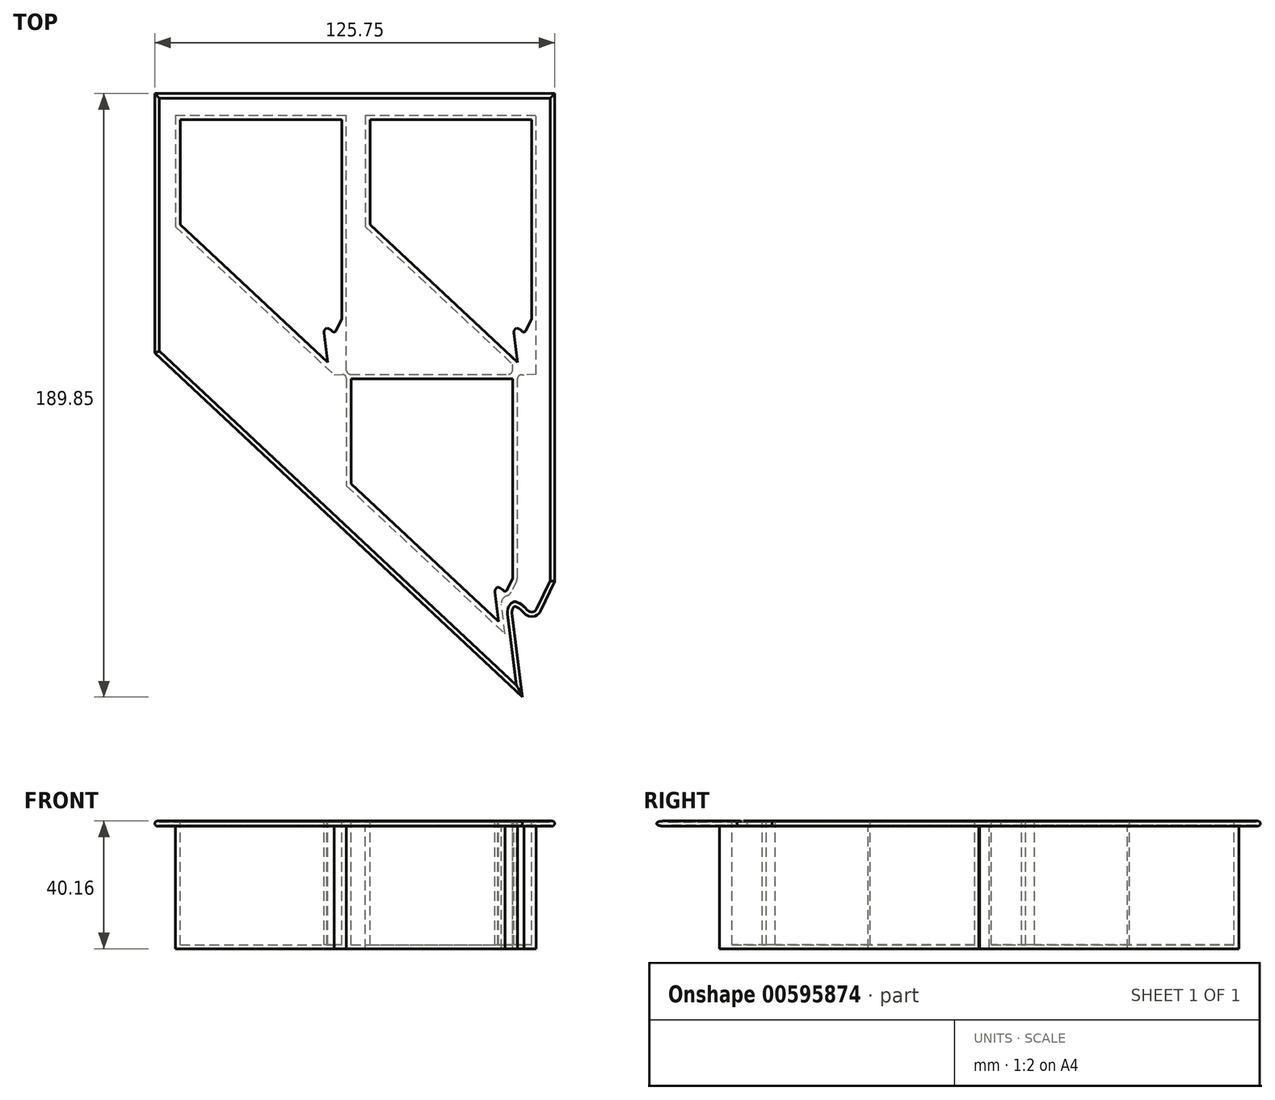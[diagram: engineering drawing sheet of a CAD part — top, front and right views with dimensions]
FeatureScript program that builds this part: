
annotation { "Feature Type Name" : "Feature", "Feature Type Description" : "" }
export const myFeature = defineFeature(function(context is Context, id is Id, definition is map)
    precondition{}
    {
        {
            var Q0;
            Q0=qCreatedBy(makeId("Top.planeOp"),FACE);
            var sketch = newSketch(context, id + "F0", { "sketchPlane" : qUnion([Q0])});
            skLineSegment(sketch, "E0.0.1.0", {"start": v(5.08, 168.36) * mm, "end": v(5.08, 133.3) * mm});
            skLineSegment(sketch, "E0.0.1.1", {"start": v(5.08, 133.3) * mm, "end": v(54.96, 86.61) * mm});
            skLineSegment(sketch, "E0.0.1.2", {"start": v(6.58, 133.95) * mm, "end": v(52.95, 90.55) * mm});
            skLineSegment(sketch, "E0.0.1.3", {"start": v(6.58, 166.86) * mm, "end": v(57.33, 166.86) * mm});
            skLineSegment(sketch, "E0.0.1.4", {"start": v(57.33, 104.15) * mm, "end": v(57.33, 166.86) * mm});
            skLineSegment(sketch, "E0.0.1.5", {"start": v(6.58, 166.86) * mm, "end": v(6.58, 133.95) * mm});
            skLineSegment(sketch, "E0.0.1.6", {"start": v(58.83, 104.4) * mm, "end": v(58.83, 168.36) * mm});
            skLineSegment(sketch, "E0.0.1.7", {"start": v(5.08, 168.36) * mm, "end": v(58.83, 168.36) * mm});
            skPoint(sketch, "E0.0.1.8", {"position": v(51.57, 101.26) * mm});
            skPoint(sketch, "E0.0.1.9", {"position": v(53.31, 101.48) * mm});
            skPoint(sketch, "E0.0.1.10", {"position": v(58.83, 103.8) * mm});
            skLineSegment(sketch, "E0.0.1.11", {"start": v(54.96, 86.61) * mm, "end": v(53.77, 95.92) * mm});
            skLineSegment(sketch, "E0.0.1.12", {"start": v(52.95, 90.55) * mm, "end": v(51.76, 99.78) * mm});
            skPoint(sketch, "E0.0.1.13", {"position": v(53, 101.9) * mm});
            skPoint(sketch, "E0.0.1.14", {"position": v(55.08, 99.52) * mm});
            skArc(sketch, "E0.0.1.15", {"start": v(55.55, 98.67) * mm, "mid": v(54.15, 97.62) * mm, "end": v(53.77, 95.92) * mm});
            skArc(sketch, "E0.0.1.16", {"start": v(53.06, 101.45) * mm, "mid": v(52.06, 100.88) * mm, "end": v(51.76, 99.78) * mm});
            skLineSegment(sketch, "E0.0.1.17", {"start": v(58.57, 103.28) * mm, "end": v(56.89, 99.82) * mm});
            skArc(sketch, "E0.0.1.18", {"start": v(58.57, 103.28) * mm, "mid": v(58.76, 103.82) * mm, "end": v(58.83, 104.4) * mm});
            skArc(sketch, "E0.0.1.19", {"start": v(54.13, 100.58) * mm, "mid": v(53.2, 101.2) * mm, "end": v(52.1, 101.33) * mm});
            skArc(sketch, "E0.0.1.20", {"start": v(55.55, 98.67) * mm, "mid": v(56.34, 99.1) * mm, "end": v(56.89, 99.82) * mm});
            skLineSegment(sketch, "E0.0.1.21", {"start": v(52.1, 101.33) * mm, "end": v(53.06, 101.45) * mm});
            skArc(sketch, "E0.0.1.22", {"start": v(54.37, 100.3) * mm, "mid": v(55, 100.08) * mm, "end": v(55.54, 100.47) * mm});
            skLineSegment(sketch, "E0.0.1.23", {"start": v(57.33, 104.15) * mm, "end": v(55.54, 100.47) * mm});
            skLineSegment(sketch, "E0.0.1.24", {"start": v(54.13, 100.58) * mm, "end": v(54.37, 100.3) * mm});
            skLineSegment(sketch, "E0.1.0.0", {"start": v(58.83, 85.48) * mm, "end": v(58.83, 51.77) * mm});
            skLineSegment(sketch, "E0.1.0.1", {"start": v(58.83, 51.77) * mm, "end": v(108.71, 5.08) * mm});
            skLineSegment(sketch, "E0.1.0.2", {"start": v(60.33, 52.42) * mm, "end": v(106.7, 9.02) * mm});
            skLineSegment(sketch, "E0.1.0.3", {"start": v(60.33, 85.33) * mm, "end": v(111.08, 85.33) * mm});
            skLineSegment(sketch, "E0.1.0.4", {"start": v(111.08, 22.62) * mm, "end": v(111.08, 85.33) * mm});
            skLineSegment(sketch, "E0.1.0.5", {"start": v(60.33, 85.33) * mm, "end": v(60.33, 52.42) * mm});
            skLineSegment(sketch, "E0.1.0.6", {"start": v(112.58, 22.86) * mm, "end": v(112.58, 85.34) * mm});
            skLineSegment(sketch, "E0.1.0.7", {"start": v(60.1, 86.82) * mm, "end": v(109.8, 86.82) * mm});
            skPoint(sketch, "E0.1.0.8", {"position": v(105.32, 19.73) * mm});
            skPoint(sketch, "E0.1.0.9", {"position": v(107.06, 19.95) * mm});
            skPoint(sketch, "E0.1.0.10", {"position": v(112.58, 22.28) * mm});
            skLineSegment(sketch, "E0.1.0.11", {"start": v(108.71, 5.08) * mm, "end": v(107.52, 14.38) * mm});
            skLineSegment(sketch, "E0.1.0.12", {"start": v(106.7, 9.02) * mm, "end": v(105.51, 18.24) * mm});
            skPoint(sketch, "E0.1.0.13", {"position": v(106.75, 20.38) * mm});
            skPoint(sketch, "E0.1.0.14", {"position": v(108.83, 18) * mm});
            skArc(sketch, "E0.1.0.15", {"start": v(109.3, 17.14) * mm, "mid": v(107.9, 16.09) * mm, "end": v(107.52, 14.38) * mm});
            skArc(sketch, "E0.1.0.16", {"start": v(106.8, 19.92) * mm, "mid": v(105.81, 19.35) * mm, "end": v(105.51, 18.24) * mm});
            skLineSegment(sketch, "E0.1.0.17", {"start": v(112.32, 21.75) * mm, "end": v(110.64, 18.28) * mm});
            skArc(sketch, "E0.1.0.18", {"start": v(112.32, 21.75) * mm, "mid": v(112.51, 22.3) * mm, "end": v(112.58, 22.86) * mm});
            skArc(sketch, "E0.1.0.19", {"start": v(107.88, 19.05) * mm, "mid": v(106.96, 19.67) * mm, "end": v(105.86, 19.8) * mm});
            skArc(sketch, "E0.1.0.20", {"start": v(109.3, 17.14) * mm, "mid": v(110.09, 17.57) * mm, "end": v(110.64, 18.28) * mm});
            skLineSegment(sketch, "E0.1.0.21", {"start": v(105.86, 19.8) * mm, "end": v(106.8, 19.92) * mm});
            skArc(sketch, "E0.1.0.22", {"start": v(108.12, 18.77) * mm, "mid": v(108.75, 18.55) * mm, "end": v(109.3, 18.94) * mm});
            skLineSegment(sketch, "E0.1.0.23", {"start": v(111.08, 22.62) * mm, "end": v(109.3, 18.94) * mm});
            skLineSegment(sketch, "E0.1.0.24", {"start": v(107.88, 19.05) * mm, "end": v(108.12, 18.77) * mm});
            skLineSegment(sketch, "E0.1.1.0", {"start": v(64.77, 168.36) * mm, "end": v(64.77, 133.3) * mm});
            skLineSegment(sketch, "E0.1.1.1", {"start": v(64.77, 133.3) * mm, "end": v(114.65, 86.61) * mm});
            skLineSegment(sketch, "E0.1.1.2", {"start": v(66.27, 133.95) * mm, "end": v(112.64, 90.55) * mm});
            skLineSegment(sketch, "E0.1.1.3", {"start": v(66.27, 166.86) * mm, "end": v(117.02, 166.86) * mm});
            skLineSegment(sketch, "E0.1.1.4", {"start": v(117.02, 104.15) * mm, "end": v(117.02, 166.86) * mm});
            skLineSegment(sketch, "E0.1.1.5", {"start": v(66.27, 166.86) * mm, "end": v(66.27, 133.95) * mm});
            skLineSegment(sketch, "E0.1.1.6", {"start": v(118.52, 104.4) * mm, "end": v(118.52, 168.36) * mm});
            skLineSegment(sketch, "E0.1.1.7", {"start": v(64.77, 168.36) * mm, "end": v(118.52, 168.36) * mm});
            skPoint(sketch, "E0.1.1.8", {"position": v(111.26, 101.26) * mm});
            skPoint(sketch, "E0.1.1.9", {"position": v(113, 101.48) * mm});
            skPoint(sketch, "E0.1.1.10", {"position": v(118.52, 103.8) * mm});
            skLineSegment(sketch, "E0.1.1.11", {"start": v(114.65, 86.61) * mm, "end": v(113.46, 95.92) * mm});
            skLineSegment(sketch, "E0.1.1.12", {"start": v(112.64, 90.55) * mm, "end": v(111.45, 99.78) * mm});
            skPoint(sketch, "E0.1.1.13", {"position": v(112.69, 101.9) * mm});
            skPoint(sketch, "E0.1.1.14", {"position": v(114.77, 99.52) * mm});
            skArc(sketch, "E0.1.1.15", {"start": v(115.24, 98.67) * mm, "mid": v(113.84, 97.62) * mm, "end": v(113.46, 95.92) * mm});
            skArc(sketch, "E0.1.1.16", {"start": v(112.75, 101.45) * mm, "mid": v(111.75, 100.88) * mm, "end": v(111.45, 99.78) * mm});
            skLineSegment(sketch, "E0.1.1.17", {"start": v(118.26, 103.28) * mm, "end": v(116.58, 99.82) * mm});
            skArc(sketch, "E0.1.1.18", {"start": v(118.26, 103.28) * mm, "mid": v(118.45, 103.82) * mm, "end": v(118.52, 104.4) * mm});
            skArc(sketch, "E0.1.1.19", {"start": v(113.82, 100.58) * mm, "mid": v(112.9, 101.2) * mm, "end": v(111.8, 101.33) * mm});
            skArc(sketch, "E0.1.1.20", {"start": v(115.24, 98.67) * mm, "mid": v(116.03, 99.1) * mm, "end": v(116.58, 99.82) * mm});
            skLineSegment(sketch, "E0.1.1.21", {"start": v(111.8, 101.33) * mm, "end": v(112.75, 101.45) * mm});
            skArc(sketch, "E0.1.1.22", {"start": v(114.06, 100.3) * mm, "mid": v(114.7, 100.08) * mm, "end": v(115.23, 100.47) * mm});
            skLineSegment(sketch, "E0.1.1.23", {"start": v(117.02, 104.15) * mm, "end": v(115.23, 100.47) * mm});
            skLineSegment(sketch, "E0.1.1.24", {"start": v(113.82, 100.58) * mm, "end": v(114.06, 100.3) * mm});
            skLineSegment(sketch, "E1", {"start": v(58.83, 88.1) * mm, "end": v(58.83, 104.4) * mm});
            skLineSegment(sketch, "E2", {"start": v(118.52, 86.82) * mm, "end": v(118.52, 104.4) * mm});
            skLineSegment(sketch, "E3", {"start": v(178.2, 86.82) * mm, "end": v(178.2, 104.4) * mm});
            skLineSegment(sketch, "E4", {"start": v(174.34, 86.82) * mm, "end": v(174.34, 86.61) * mm});
            skLineSegment(sketch, "E5", {"start": v(118.52, 86.82) * mm, "end": v(114.65, 86.61) * mm});
            skLineSegment(sketch, "E6", {"start": v(113.85, 86.61) * mm, "end": v(114.65, 86.61) * mm});
            skLineSegment(sketch, "E7", {"start": v(111.06, 88.1) * mm, "end": v(111.06, 89.98) * mm});
            skLineSegment(sketch, "E8", {"start": v(54.96, 86.61) * mm, "end": v(57.5, 86.75) * mm});
            skPoint(sketch, "E9.visualSharp", {"position": v(58.83, 86.82) * mm});
            skArc(sketch, "E9.filletArc", {"start": v(58.83, 88.1) * mm, "mid": v(59.2, 87.2) * mm, "end": v(60.1, 86.82) * mm});
            skArc(sketch, "E10.filletArc", {"start": v(58.83, 85.48) * mm, "mid": v(58.43, 86.4) * mm, "end": v(57.5, 86.75) * mm});
            skArc(sketch, "E11.filletArc", {"start": v(109.8, 86.82) * mm, "mid": v(110.7, 87.2) * mm, "end": v(111.06, 88.1) * mm});
            skPoint(sketch, "E12.newPointA", {"position": v(112.58, 86.61) * mm});
            skPoint(sketch, "E12.newPointB", {"position": v(112.58, 86.82) * mm});
            skArc(sketch, "E12.filletArc", {"start": v(113.85, 86.61) * mm, "mid": v(112.95, 86.24) * mm, "end": v(112.58, 85.34) * mm});
            skSolve(sketch);
        }
        {
            var Q0;
            Q0=qCreatedBy(makeId("Top.planeOp"),FACE);
            var sketch = newSketch(context, id + "F1", { "sketchPlane" : qUnion([Q0])});
            skLineSegment(sketch, "E13", {"start": v(122.91, 173.7) * mm, "end": v(122.91, 21.91) * mm});
            skLineSegment(sketch, "E14", {"start": v(122.91, 21.91) * mm, "end": v(118.6, 13.03) * mm});
            skLineSegment(sketch, "E15", {"start": v(109.42, 11.41) * mm, "end": v(112.3, -10.99) * mm});
            skLineSegment(sketch, "E16", {"start": v(112.3, -10.99) * mm, "end": v(0, 94.11) * mm});
            skLineSegment(sketch, "E17", {"start": v(0, 94.11) * mm, "end": v(0, 173.7) * mm});
            skLineSegment(sketch, "E18", {"start": v(0, 173.7) * mm, "end": v(122.91, 173.7) * mm});
            skFitSpline(sketch, "E19", {"points": [v(109.42, 11.41) * mm, v(110.69, 14.8) * mm, v(112.4, 15.15) * mm, v(114.95, 13.46) * mm, v(115.81, 12.54) * mm, v(117.4, 12.03) * mm, v(118.6, 13.03) * mm], "startDerivative": vector(-2.44, 18.96) * mm, "endDerivative": vector(5.18, 10.64) * mm});
            skSolve(sketch);
        }
        {
            var Q0;
            Q0=qCreatedBy(makeId("Front.planeOp"),FACE);
            cPlane(context, id + "F2", {"entities" : qUnion([Q0]), "cplaneType" : CPlaneType.OFFSET, "offset" : 103.89 * mm, "oppositeDirection" : true, "width" : 152.4 * mm, "height" : 152.4 * mm});
        }
        {
            var Q0;
            Q0=qCreatedBy(id+"F2.planeOp",FACE);
            var sketch = newSketch(context, id + "F3", { "sketchPlane" : qUnion([Q0])});
            skPoint(sketch, "E20.0", {"position": v(0, 0) * mm});
            skArc(sketch, "E21", {"start": v(-0.05, 0.52) * mm, "mid": v(-1.42, 0) * mm, "end": v(-0.05, -0.52) * mm});
            skLineSegment(sketch, "E22", {"start": v(-0.01, 0.5) * mm, "end": v(0, 0.5) * mm});
            skLineSegment(sketch, "E23", {"start": v(0, 0.5) * mm, "end": v(0, -0.5) * mm});
            skLineSegment(sketch, "E24", {"start": v(0, -0.5) * mm, "end": v(-0.01, -0.5) * mm});
            skPoint(sketch, "E25.visualSharp", {"position": v(-0.03, 0.5) * mm});
            skArc(sketch, "E25.filletArc", {"start": v(-0.05, 0.52) * mm, "mid": v(-0.03, 0.51) * mm, "end": v(-0.01, 0.5) * mm});
            skPoint(sketch, "E26.visualSharp", {"position": v(-1.24, -0.5) * mm});
            skArc(sketch, "E26.filletArc", {"start": v(-0.01, -0.5) * mm, "mid": v(-0.03, -0.51) * mm, "end": v(-0.05, -0.52) * mm});
            skSolve(sketch);
        }
        {
            var Q0;
            Q0=makeQuery(id+"F3.imprint","IMPRINT",FACE,{"disambiguationData":[TD([[makeQuery(id+"F3.imprint","IMPRINT",EDGE,{"derivedFrom":sQuery(id+"F3.wireOp",EDGE,"E21")}),1.0]])]});
            var Q1;
            Q1=sQuery(id+"F1.wireOp",EDGE,"E17");
            var Q2;
            Q2=sQuery(id+"F1.wireOp",EDGE,"E16");
            var Q3;
            Q3=sQuery(id+"F1.wireOp",EDGE,"E15");
            var Q4;
            Q4=sQuery(id+"F1.wireOp",EDGE,"E19");
            var Q5;
            Q5=sQuery(id+"F1.wireOp",EDGE,"E14");
            var Q6;
            Q6=sQuery(id+"F1.wireOp",EDGE,"E13");
            var Q7;
            Q7=sQuery(id+"F1.wireOp",EDGE,"E18");
            sweep(context, id + "F4", {"profiles" : qUnion([Q0]), "path" : qUnion([Q1, Q2, Q3, Q4, Q5, Q6, Q7])});
        }
        {
            var Q0;
            Q0=makeQuery(id+"F4.opSweep","SWEPT_EDGE",EDGE,{"disambiguationData":[OSD([sQuery(id+"F1.wireOp",EDGE,"E18"),sQuery(id+"F3.wireOp",EDGE,"E22"),sQuery(id+"F3.wireOp",EDGE,"E23")])]});
            cPlane(context, id + "F5", {"entities" : qUnion([Q0]), "cplaneType" : CPlaneType.LINE_ANGLE, "offset" : 25.4 * mm, "angle" : 90 * degree, "width" : 152.4 * mm, "height" : 152.4 * mm});
        }
        {
            var Q0;
            Q0=makeQuery(id+"F1.imprint","IMPRINT",FACE,{"disambiguationData":[TD([[makeQuery(id+"F1.imprint","IMPRINT",EDGE,{"derivedFrom":sQuery(id+"F1.wireOp",EDGE,"E13")}),-1.0]])]});
            extrude(context, id + "F6", {"entities" : qUnion([Q0]), "operationType" : NewBodyOperationType.ADD, "depth" : 1 * mm, "offsetDistance" : 25.4 * mm, "symmetric" : true});
        }
        {
            var Q0;
            {var subQ6=sQuery(id+"F0.wireOp",EDGE,"E0.0.1.0");Q0=makeQuery(id+"F0.imprint","IMPRINT",FACE,{"disambiguationData":[TD([[makeQuery(id+"F0.imprint","IMPRINT",EDGE,{"derivedFrom":subQ6}),1.0]])]});}
            var Q1;
            {var subQ6=sQuery(id+"F0.wireOp",EDGE,"E0.1.1.0");Q1=makeQuery(id+"F0.imprint","IMPRINT",FACE,{"disambiguationData":[TD([[makeQuery(id+"F0.imprint","IMPRINT",EDGE,{"derivedFrom":subQ6}),1.0]])]});}
            var Q2;
            {var subQ3=sQuery(id+"F0.wireOp",EDGE,"E0.1.0.0");Q2=makeQuery(id+"F0.imprint","IMPRINT",FACE,{"disambiguationData":[TD([[makeQuery(id+"F0.imprint","IMPRINT",EDGE,{"derivedFrom":subQ3}),1.0]])]});}
            var Q3;
            Q3=makeQuery(id+"F0.imprint","IMPRINT",FACE,{"disambiguationData":[TD([[makeQuery(id+"F0.imprint","IMPRINT",EDGE,{"derivedFrom":sQuery(id+"F0.wireOp",EDGE,"E0.1.1.2")}),1.0]])]});
            var Q4;
            Q4=makeQuery(id+"F0.imprint","IMPRINT",FACE,{"disambiguationData":[TD([[makeQuery(id+"F0.imprint","IMPRINT",EDGE,{"derivedFrom":sQuery(id+"F0.wireOp",EDGE,"E0.0.1.2")}),1.0]])]});
            var Q5;
            Q5=makeQuery(id+"F0.imprint","IMPRINT",FACE,{"disambiguationData":[TD([[makeQuery(id+"F0.imprint","IMPRINT",EDGE,{"derivedFrom":sQuery(id+"F0.wireOp",EDGE,"E0.1.0.2")}),1.0]])]});
            var Q6;
            {var subQ0=sQuery(id+"F0.wireOp",EDGE,"E0.0.1.21");Q6=makeQuery(id+"F0.imprint","IMPRINT",FACE,{"disambiguationData":[TD([[makeQuery(id+"F0.imprint","IMPRINT",EDGE,{"derivedFrom":subQ0}),-1.0]])]});}
            var Q7;
            {var subQ0=sQuery(id+"F0.wireOp",EDGE,"E0.1.1.21");Q7=makeQuery(id+"F0.imprint","IMPRINT",FACE,{"disambiguationData":[TD([[makeQuery(id+"F0.imprint","IMPRINT",EDGE,{"derivedFrom":subQ0}),-1.0]])]});}
            var Q8;
            {var subQ0=sQuery(id+"F0.wireOp",EDGE,"E0.1.0.21");Q8=makeQuery(id+"F0.imprint","IMPRINT",FACE,{"disambiguationData":[TD([[makeQuery(id+"F0.imprint","IMPRINT",EDGE,{"derivedFrom":subQ0}),-1.0]])]});}
            var Q9;
            {var subQ0=sQuery(id+"F0.wireOp",EDGE,"E0.0.1.15");Q9=makeQuery(id+"F0.imprint","IMPRINT",FACE,{"disambiguationData":[TD([[makeQuery(id+"F0.imprint","IMPRINT",EDGE,{"derivedFrom":subQ0}),1.0]])]});}
            var Q10;
            {var subQ0=sQuery(id+"F0.wireOp",EDGE,"E0.1.1.15");Q10=makeQuery(id+"F0.imprint","IMPRINT",FACE,{"disambiguationData":[TD([[makeQuery(id+"F0.imprint","IMPRINT",EDGE,{"derivedFrom":subQ0}),1.0]])]});}
            var Q11;
            {var subQ0=sQuery(id+"F0.wireOp",EDGE,"Uk30h5Cc-5NcR-Sx4F-vrMV-0Ktg2mvz4VKh");Q11=makeQuery(id+"F0.imprint","IMPRINT",FACE,{"disambiguationData":[TD([[makeQuery(id+"F0.imprint","IMPRINT",EDGE,{"derivedFrom":subQ0}),1.0]])]});}
            extrude(context, id + "F7", {"entities" : qUnion([Q0, Q1, Q2, Q3, Q4, Q5, Q6, Q7, Q8, Q9, Q10, Q11]), "operationType" : NewBodyOperationType.ADD, "oppositeDirection" : true, "depth" : 39.37 * mm, "offsetDistance" : 25.4 * mm});
        }
        {
            var Q0;
            Q0=makeQuery(id+"F0.imprint","IMPRINT",FACE,{"disambiguationData":[TD([[makeQuery(id+"F0.imprint","IMPRINT",EDGE,{"derivedFrom":sQuery(id+"F0.wireOp",EDGE,"E0.1.0.2")}),1.0]])]});
            var Q1;
            {var subQ0=sQuery(id+"F0.wireOp",EDGE,"E0.1.0.21");Q1=makeQuery(id+"F0.imprint","IMPRINT",FACE,{"disambiguationData":[TD([[makeQuery(id+"F0.imprint","IMPRINT",EDGE,{"derivedFrom":subQ0}),-1.0]])]});}
            var Q2;
            {var subQ0=sQuery(id+"F0.wireOp",EDGE,"E0.1.1.21");Q2=makeQuery(id+"F0.imprint","IMPRINT",FACE,{"disambiguationData":[TD([[makeQuery(id+"F0.imprint","IMPRINT",EDGE,{"derivedFrom":subQ0}),-1.0]])]});}
            var Q3;
            Q3=makeQuery(id+"F0.imprint","IMPRINT",FACE,{"disambiguationData":[TD([[makeQuery(id+"F0.imprint","IMPRINT",EDGE,{"derivedFrom":sQuery(id+"F0.wireOp",EDGE,"E0.1.1.2")}),1.0]])]});
            var Q4;
            {var subQ0=sQuery(id+"F0.wireOp",EDGE,"E0.0.1.21");Q4=makeQuery(id+"F0.imprint","IMPRINT",FACE,{"disambiguationData":[TD([[makeQuery(id+"F0.imprint","IMPRINT",EDGE,{"derivedFrom":subQ0}),-1.0]])]});}
            var Q5;
            Q5=makeQuery(id+"F0.imprint","IMPRINT",FACE,{"disambiguationData":[TD([[makeQuery(id+"F0.imprint","IMPRINT",EDGE,{"derivedFrom":sQuery(id+"F0.wireOp",EDGE,"E0.0.1.2")}),1.0]])]});
            extrude(context, id + "F8", {"entities" : qUnion([Q0, Q1, Q2, Q3, Q4, Q5]), "operationType" : NewBodyOperationType.REMOVE, "oppositeDirection" : true, "depth" : 38.1 * mm, "offsetDistance" : 25.4 * mm, "hasSecondDirection" : true, "secondDirectionOppositeDirection" : false, "secondDirectionDepth" : 25.4 * mm});
        }
    });
